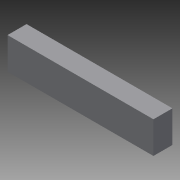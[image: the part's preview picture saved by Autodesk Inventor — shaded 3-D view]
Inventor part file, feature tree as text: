
AUTODESK INVENTOR PART (.ipt)
format: ipt  version: 2013 (Build 170138000, 138)  size: 72,192 bytes
history: native  units: in
note: dims shown in document units (in); Inventor stores cm internally (conversion verified against a paired STEP export)
features: extrude x1, sketch x1
ambient origin geometry x8: Origin, YZ Plane, XZ Plane, XY Plane, X Axis, Y Axis, Z Axis, Center Point
bodies: Solid1 (feature_tree)
feature tree (2):
  extrude  "Extrusion1"  Depth=1.0in
  sketch  "Sketch1"  dims[d0=3.625in d1=1.0in d2=5.0in d3=0.0in d4=23.0in d5=90.0deg d6=5.0in d7=90.0deg d8=3.0in d9=0.0in]
